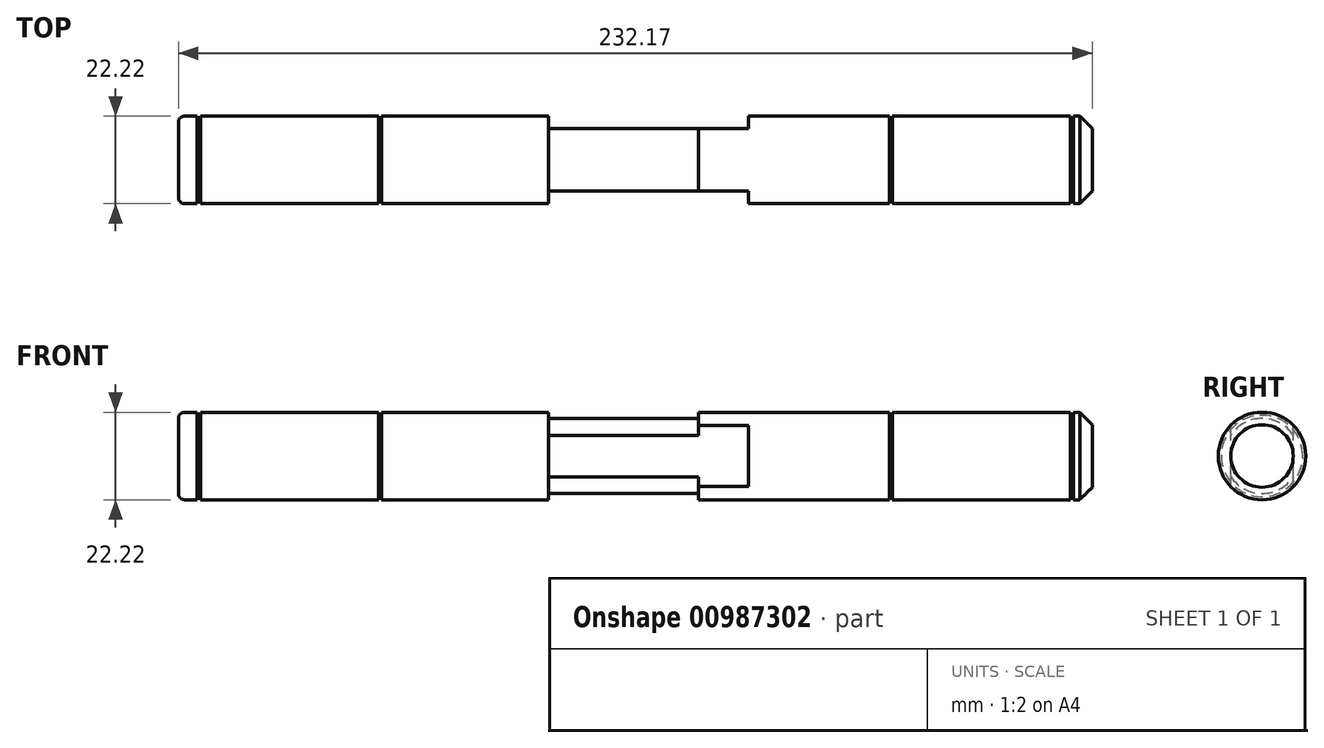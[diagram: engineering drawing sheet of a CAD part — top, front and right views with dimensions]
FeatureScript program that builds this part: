
annotation { "Feature Type Name" : "Feature", "Feature Type Description" : "" }
export const myFeature = defineFeature(function(context is Context, id is Id, definition is map)
    precondition{}
    {
        {
            var Q0;
            Q0=qCreatedBy(makeId("Right.planeOp"),FACE);
            var sketch = newSketch(context, id + "F0", { "sketchPlane" : qUnion([Q0])});
            skArc(sketch, "E0", {"start": v(7.94, 5.27) * mm, "mid": v(0, 9.52) * mm, "end": v(-7.94, 5.27) * mm});
            skPoint(sketch, "E1.end.orphan", {"position": v(8.87, -3.47) * mm});
            skPoint(sketch, "E1.start.orphan", {"position": v(8.87, 3.47) * mm});
            skLineSegment(sketch, "E2", {"start": v(-7.94, -5.27) * mm, "end": v(-7.94, 5.27) * mm});
            skLineSegment(sketch, "E3", {"start": v(7.94, -5.27) * mm, "end": v(7.94, 5.27) * mm});
            skArc(sketch, "E4.trimOffspring", {"start": v(-7.94, -5.27) * mm, "mid": v(0, -9.53) * mm, "end": v(7.94, -5.27) * mm});
            skSolve(sketch);
        }
        {
            var Q0;
            Q0=makeQuery(id+"F0.imprint","IMPRINT",FACE,{"disambiguationData":[TD([[makeQuery(id+"F0.imprint","IMPRINT",EDGE,{"derivedFrom":sQuery(id+"F0.wireOp",EDGE,"E0")}),1.0]])]});
            extrude(context, id + "F1", {"entities" : qUnion([Q0]), "endBound" : BoundingType.SYMMETRIC, "depth" : 38.1 * mm, "offsetDistance" : 25.4 * mm});
        }
        {
            var Q0;
            Q0=makeQuery(id+"F1.opExtrude","CAP_FACE",FACE,{"disambiguationData":[OSD([sQuery(id+"F0.wireOp",EDGE,"E0"),sQuery(id+"F0.wireOp",EDGE,"E2"),sQuery(id+"F0.wireOp",EDGE,"E3"),sQuery(id+"F0.wireOp",EDGE,"E4.trimOffspring")])],"isStart":false});
            var sketch = newSketch(context, id + "F2", { "sketchPlane" : qUnion([Q0])});
            skArc(sketch, "E5", {"start": v(-7.94, -7.78) * mm, "mid": v(0, -11.11) * mm, "end": v(7.94, -7.78) * mm});
            skLineSegment(sketch, "E6", {"start": v(7.94, -7.78) * mm, "end": v(7.94, 7.78) * mm});
            skLineSegment(sketch, "E7", {"start": v(-7.94, -7.78) * mm, "end": v(-7.94, 7.78) * mm});
            skArc(sketch, "E8.trimOffspring", {"start": v(7.94, 7.78) * mm, "mid": v(0, 11.11) * mm, "end": v(-7.94, 7.78) * mm});
            skSolve(sketch);
        }
        {
            var Q0;
            Q0 = qSketchRegion(id + "F2", true);
            extrude(context, id + "F3", {"entities" : qUnion([Q0]), "operationType" : NewBodyOperationType.ADD, "depth" : 12.7 * mm, "offsetDistance" : 25.4 * mm});
        }
        {
            var Q0;
            Q0=makeQuery(id+"F3.opExtrude","CAP_FACE",FACE,{"disambiguationData":[OSD([sQuery(id+"F2.wireOp",EDGE,"E5"),sQuery(id+"F2.wireOp",EDGE,"E6"),sQuery(id+"F2.wireOp",EDGE,"E7"),sQuery(id+"F2.wireOp",EDGE,"E8.trimOffspring")])],"isStart":false});
            var sketch = newSketch(context, id + "F4", { "sketchPlane" : qUnion([Q0])});
            skCircle(sketch, "E9", {"center": v(0, 0) * mm, "radius": 11.11 * mm});
            skSolve(sketch);
        }
        {
            var Q0;
            Q0 = qSketchRegion(id + "F4", true);
            extrude(context, id + "F5", {"entities" : qUnion([Q0]), "operationType" : NewBodyOperationType.ADD, "depth" : 35.72 * mm, "offsetDistance" : 25.4 * mm});
        }
        {
            var Q0;
            Q0=makeQuery(id+"F1.opExtrude","CAP_FACE",FACE,{"disambiguationData":[OSD([sQuery(id+"F0.wireOp",EDGE,"E0"),sQuery(id+"F0.wireOp",EDGE,"E2"),sQuery(id+"F0.wireOp",EDGE,"E3"),sQuery(id+"F0.wireOp",EDGE,"E4.trimOffspring")])],"isStart":true});
            var sketch = newSketch(context, id + "F6", { "sketchPlane" : qUnion([Q0])});
            skCircle(sketch, "E10", {"center": v(0, 0) * mm, "radius": 11.11 * mm});
            skSolve(sketch);
        }
        {
            var Q0;
            Q0 = qSketchRegion(id + "F6", true);
            extrude(context, id + "F7", {"entities" : qUnion([Q0]), "operationType" : NewBodyOperationType.ADD, "depth" : 42.47 * mm, "offsetDistance" : 25.4 * mm});
        }
        {
            var Q0;
            Q0=makeQuery(id+"F5.opExtrude","CAP_FACE",FACE,{"disambiguationData":[OSD([sQuery(id+"F4.wireOp",EDGE,"E9")])],"isStart":false});
            var sketch = newSketch(context, id + "F8", { "sketchPlane" : qUnion([Q0])});
            skCircle(sketch, "E11", {"center": v(0, 0) * mm, "radius": 10.35 * mm});
            skSolve(sketch);
        }
        {
            var Q0;
            Q0 = qSketchRegion(id + "F8", true);
            extrude(context, id + "F9", {"entities" : qUnion([Q0]), "operationType" : NewBodyOperationType.ADD, "depth" : 0.79 * mm, "offsetDistance" : 25.4 * mm});
        }
        {
            var Q0;
            Q0=makeQuery(id+"F7.opExtrude","CAP_FACE",FACE,{"disambiguationData":[OSD([sQuery(id+"F6.wireOp",EDGE,"E10")])],"isStart":false});
            var sketch = newSketch(context, id + "F10", { "sketchPlane" : qUnion([Q0])});
            skCircle(sketch, "E12", {"center": v(0, 0) * mm, "radius": 10.35 * mm});
            skSolve(sketch);
        }
        {
            var Q0;
            Q0 = qSketchRegion(id + "F10", true);
            extrude(context, id + "F11", {"entities" : qUnion([Q0]), "operationType" : NewBodyOperationType.ADD, "depth" : 0.79 * mm, "offsetDistance" : 25.4 * mm});
        }
        {
            var Q0;
            Q0=makeQuery(id+"F11.opExtrude","CAP_FACE",FACE,{"disambiguationData":[OSD([sQuery(id+"F10.wireOp",EDGE,"E12")])],"isStart":false});
            var sketch = newSketch(context, id + "F12", { "sketchPlane" : qUnion([Q0])});
            skCircle(sketch, "E13", {"center": v(0, 0) * mm, "radius": 11.11 * mm});
            skSolve(sketch);
        }
        {
            var Q0;
            Q0 = qSketchRegion(id + "F12", true);
            extrude(context, id + "F13", {"entities" : qUnion([Q0]), "operationType" : NewBodyOperationType.ADD, "depth" : 45.24 * mm, "offsetDistance" : 25.4 * mm});
        }
        {
            var Q0;
            Q0=makeQuery(id+"F13.opExtrude","CAP_FACE",FACE,{"disambiguationData":[OSD([sQuery(id+"F12.wireOp",EDGE,"E13")])],"isStart":false});
            var sketch = newSketch(context, id + "F14", { "sketchPlane" : qUnion([Q0])});
            skCircle(sketch, "E14", {"center": v(0, 0) * mm, "radius": 10.35 * mm});
            skSolve(sketch);
        }
        {
            var Q0;
            Q0 = qSketchRegion(id + "F14", true);
            extrude(context, id + "F15", {"entities" : qUnion([Q0]), "operationType" : NewBodyOperationType.ADD, "depth" : 0.79 * mm, "offsetDistance" : 25.4 * mm});
        }
        {
            var Q0;
            Q0=makeQuery(id+"F15.opExtrude","CAP_FACE",FACE,{"disambiguationData":[OSD([sQuery(id+"F14.wireOp",EDGE,"E14")])],"isStart":false});
            var sketch = newSketch(context, id + "F16", { "sketchPlane" : qUnion([Q0])});
            skCircle(sketch, "E15", {"center": v(0, 0) * mm, "radius": 11.11 * mm});
            skSolve(sketch);
        }
        {
            var Q0;
            Q0 = qSketchRegion(id + "F16", true);
            extrude(context, id + "F17", {"entities" : qUnion([Q0]), "operationType" : NewBodyOperationType.ADD, "depth" : 4.78 * mm, "offsetDistance" : 25.4 * mm});
        }
        {
            var Q0;
            Q0=makeQuery(id+"F17.opExtrude","CAP_EDGE",EDGE,{"disambiguationData":[OSD([sQuery(id+"F16.wireOp",EDGE,"E15")])],"isStart":false});
            fillet(context, id + "F18", {"entities" : qUnion([Q0]), "radius" : 1.52 * mm, "tangentPropagation" : true, "allowEdgeOverflow" : false});
        }
        {
            var Q0;
            Q0=makeQuery(id+"F9.opExtrude","CAP_FACE",FACE,{"disambiguationData":[OSD([sQuery(id+"F8.wireOp",EDGE,"E11")])],"isStart":false});
            var sketch = newSketch(context, id + "F19", { "sketchPlane" : qUnion([Q0])});
            skCircle(sketch, "E16", {"center": v(0, 0) * mm, "radius": 11.11 * mm});
            skSolve(sketch);
        }
        {
            var Q0;
            Q0 = qSketchRegion(id + "F19", true);
            extrude(context, id + "F20", {"entities" : qUnion([Q0]), "operationType" : NewBodyOperationType.ADD, "depth" : 45.24 * mm, "offsetDistance" : 25.4 * mm});
        }
        {
            var Q0;
            Q0=makeQuery(id+"F20.opExtrude","CAP_FACE",FACE,{"disambiguationData":[OSD([sQuery(id+"F19.wireOp",EDGE,"E16")])],"isStart":false});
            var sketch = newSketch(context, id + "F21", { "sketchPlane" : qUnion([Q0])});
            skCircle(sketch, "E17", {"center": v(0, 0) * mm, "radius": 10.35 * mm});
            skSolve(sketch);
        }
        {
            var Q0;
            Q0 = qSketchRegion(id + "F21", true);
            extrude(context, id + "F22", {"entities" : qUnion([Q0]), "operationType" : NewBodyOperationType.ADD, "depth" : 0.79 * mm, "offsetDistance" : 25.4 * mm});
        }
        {
            var Q0;
            Q0=makeQuery(id+"F22.opExtrude","CAP_FACE",FACE,{"disambiguationData":[OSD([sQuery(id+"F21.wireOp",EDGE,"E17")])],"isStart":false});
            var sketch = newSketch(context, id + "F23", { "sketchPlane" : qUnion([Q0])});
            skCircle(sketch, "E18", {"center": v(0, 0) * mm, "radius": 11.11 * mm});
            skSolve(sketch);
        }
        {
            var Q0;
            Q0 = qSketchRegion(id + "F23", true);
            extrude(context, id + "F24", {"entities" : qUnion([Q0]), "operationType" : NewBodyOperationType.ADD, "depth" : 4.78 * mm, "offsetDistance" : 25.4 * mm});
        }
        {
            var Q0;
            Q0=makeQuery(id+"F24.opExtrude","CAP_EDGE",EDGE,{"disambiguationData":[OSD([sQuery(id+"F23.wireOp",EDGE,"E18")])],"isStart":false});
            chamfer(context, id + "F25", {"entities" : qUnion([Q0]), "width" : 3.17 * mm, "tangentPropagation" : true});
        }
    });
